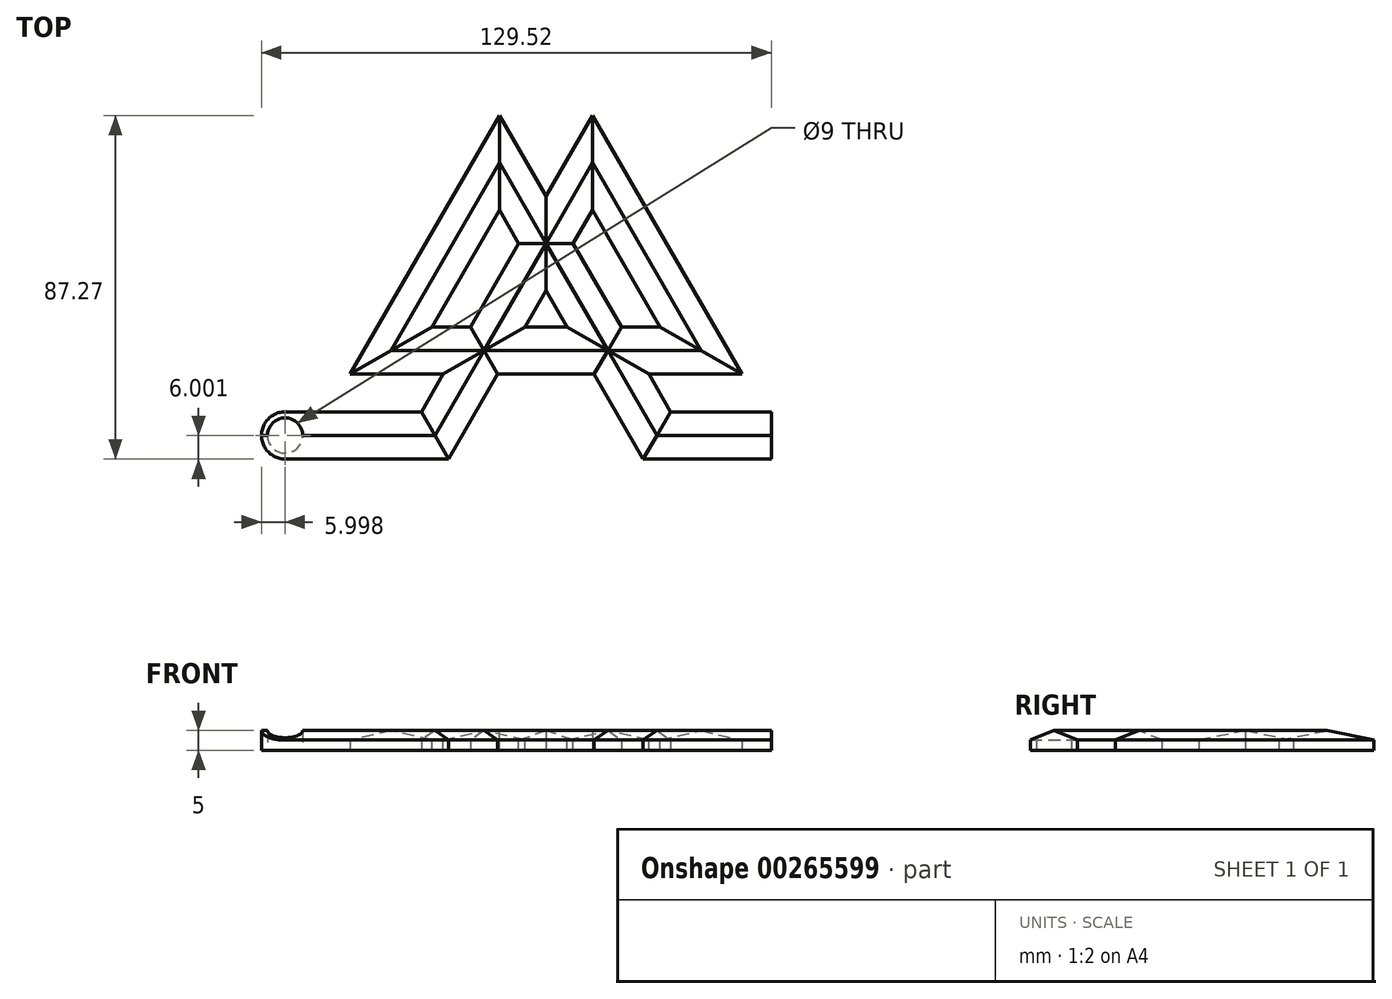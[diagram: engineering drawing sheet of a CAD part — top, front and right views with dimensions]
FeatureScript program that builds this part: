
annotation { "Feature Type Name" : "Feature", "Feature Type Description" : "" }
export const myFeature = defineFeature(function(context is Context, id is Id, definition is map)
    precondition{}
    {
        {
            var Q0;
            Q0=qCreatedBy(makeId("Top.planeOp"),FACE);
            var sketch = newSketch(context, id + "F0", { "sketchPlane" : qUnion([Q0])});
            skLineSegment(sketch, "E0", {"start": v(11.81, 20.46) * mm, "end": v(39.36, -27.25) * mm});
            skLineSegment(sketch, "E1", {"start": v(-39.36, -27.25) * mm, "end": v(-11.81, 20.46) * mm});
            skLineSegment(sketch, "E2", {"start": v(-11.81, 20.46) * mm, "end": v(28.18, -48.8) * mm});
            skLineSegment(sketch, "E3", {"start": v(28.18, -48.8) * mm, "end": v(57.26, -48.8) * mm});
            skLineSegment(sketch, "E4", {"start": v(-28.18, -48.8) * mm, "end": v(-57.26, -48.8) * mm});
            skLineSegment(sketch, "E5", {"start": v(-28.18, -48.8) * mm, "end": v(11.81, 20.46) * mm});
            skLineSegment(sketch, "E6", {"start": v(-39.36, -27.25) * mm, "end": v(0, -27.25) * mm});
            skLineSegment(sketch, "E7", {"start": v(0, -27.25) * mm, "end": v(39.36, -27.25) * mm});
            skSolve(sketch);
        }
        {
            var Q0;
            Q0=sQuery(id+"F0.wireOp",VERTEX,"E4.end");
            var Q1;
            Q1=sQuery(id+"F0.wireOp",EDGE,"E4");
            cPlane(context, id + "F1", {"entities" : qUnion([Q0, Q1]), "cplaneType" : CPlaneType.LINE_POINT, "offset" : 25 * mm, "width" : 150 * mm, "height" : 150 * mm});
        }
        {
            var Q0;
            Q0=qCreatedBy(id+"F1.planeOp",FACE);
            var sketch = newSketch(context, id + "F2", { "sketchPlane" : qUnion([Q0])});
            skLineSegment(sketch, "E8", {"start": v(48.8, 0) * mm, "end": v(42.8, -2.4) * mm});
            skLineSegment(sketch, "E9", {"start": v(54.8, -2.4) * mm, "end": v(48.8, 0) * mm});
            skLineSegment(sketch, "E10.top", {"start": v(42.8, -5) * mm, "end": v(54.8, -5) * mm});
            skLineSegment(sketch, "E10.left", {"start": v(42.8, -2.4) * mm, "end": v(42.8, -5) * mm});
            skLineSegment(sketch, "E10.right", {"start": v(54.8, -2) * mm, "end": v(54.8, -5) * mm});
            skSolve(sketch);
        }
        {
            var Q0;
            Q0=qSketchRegion(id+"F2",true);
            var Q1;
            Q1=sQuery(id+"F0.wireOp",EDGE,"E4");
            var Q2;
            Q2=sQuery(id+"F0.wireOp",EDGE,"E5");
            var Q3;
            Q3=sQuery(id+"F0.wireOp",EDGE,"E0");
            var Q4;
            Q4=sQuery(id+"F0.wireOp",EDGE,"E7");
            sweep(context, id + "F3", {"profiles" : qUnion([Q0]), "path" : qUnion([Q1, Q2, Q3, Q4])});
        }
        {
            var Q0;
            Q0=makeQuery(id+"F3.opSweep","SWEPT_BODY",BODY,{"disambiguationData":[OSD([sQuery(id+"F0.wireOp",EDGE,"E7"),sQuery(id+"F2.wireOp",EDGE,"E8"),sQuery(id+"F2.wireOp",EDGE,"Unc637DK-Oss3-EL6j-WJqW-EPe3jexTLxim"),sQuery(id+"F2.wireOp",EDGE,"E9")])]});
            var Q1;
            Q1=qCreatedBy(makeId("Right.planeOp"),FACE);
            mirror(context, id + "F4", {"operationType" : NewBodyOperationType.ADD, "entities" : qUnion([Q0]), "mirrorPlane" : qUnion([Q1])});
        }
        {
            var Q0;
            Q0=makeQuery(id+"F3.opSweep","CAP_FACE",FACE,{"disambiguationData":[OSD([sQuery(id+"F0.wireOp",VERTEX,"E4.end"),sQuery(id+"F2.wireOp",EDGE,"E8"),sQuery(id+"F2.wireOp",EDGE,"E9"),sQuery(id+"F2.wireOp",EDGE,"E10.top"),sQuery(id+"F2.wireOp",EDGE,"E10.left"),sQuery(id+"F2.wireOp",EDGE,"E10.right")])],"isStart":true});
            extrude(context, id + "F5", {"entities" : qUnion([Q0]), "operationType" : NewBodyOperationType.ADD, "depth" : 15 * mm});
        }
        {
            var Q0;
            {var subQ0=sQuery(id+"F2.wireOp",EDGE,"E10.top");var subQ1=makeQuery(id+"F3.opSweep","SWEPT_FACE",FACE,{"disambiguationData":[OSD([sQuery(id+"F0.wireOp",EDGE,"E4"),subQ0])]});Q0=makeQuery(id+"F5.boolean.opBoolean","MERGE",FACE,{"derivedFrom":[makeQuery(id+"F4.boolean.opBoolean","MERGE",FACE,{"derivedFrom":[subQ1,makeQuery(id+"F4.opPattern","COPY",FACE,{"derivedFrom":subQ1,"instanceName":"1"})]}),makeQuery(id+"F5.opExtrude","SWEPT_FACE",FACE,{"disambiguationData":[OSD([sQuery(id+"F0.wireOp",VERTEX,"E4.end"),subQ0])]})]});}
            var sketch = newSketch(context, id + "F6", { "sketchPlane" : qUnion([Q0])});
            skArc(sketch, "E11", {"start": v(-66.26, 54.8) * mm, "mid": v(-72.26, 48.8) * mm, "end": v(-66.26, 42.8) * mm});
            skPoint(sketch, "E11.centerSnap0", {"position": v(-72.26, 48.8) * mm});
            skCircle(sketch, "E12", {"center": v(-66.26, 48.8) * mm, "radius": 4.5 * mm});
            skLineSegment(sketch, "E13", {"start": v(-66.26, 54.8) * mm, "end": v(-72.26, 54.8) * mm});
            skLineSegment(sketch, "E14", {"start": v(-72.26, 54.8) * mm, "end": v(-72.26, 42.8) * mm});
            skLineSegment(sketch, "E15", {"start": v(-72.26, 42.8) * mm, "end": v(-66.26, 42.8) * mm});
            skSolve(sketch);
        }
        {
            var Q0;
            Q0 = qSketchRegion(id + "F6", true);
            extrude(context, id + "F7", {"entities" : qUnion([Q0]), "operationType" : NewBodyOperationType.REMOVE, "oppositeDirection" : true, "depth" : 25 * mm});
        }
    });
